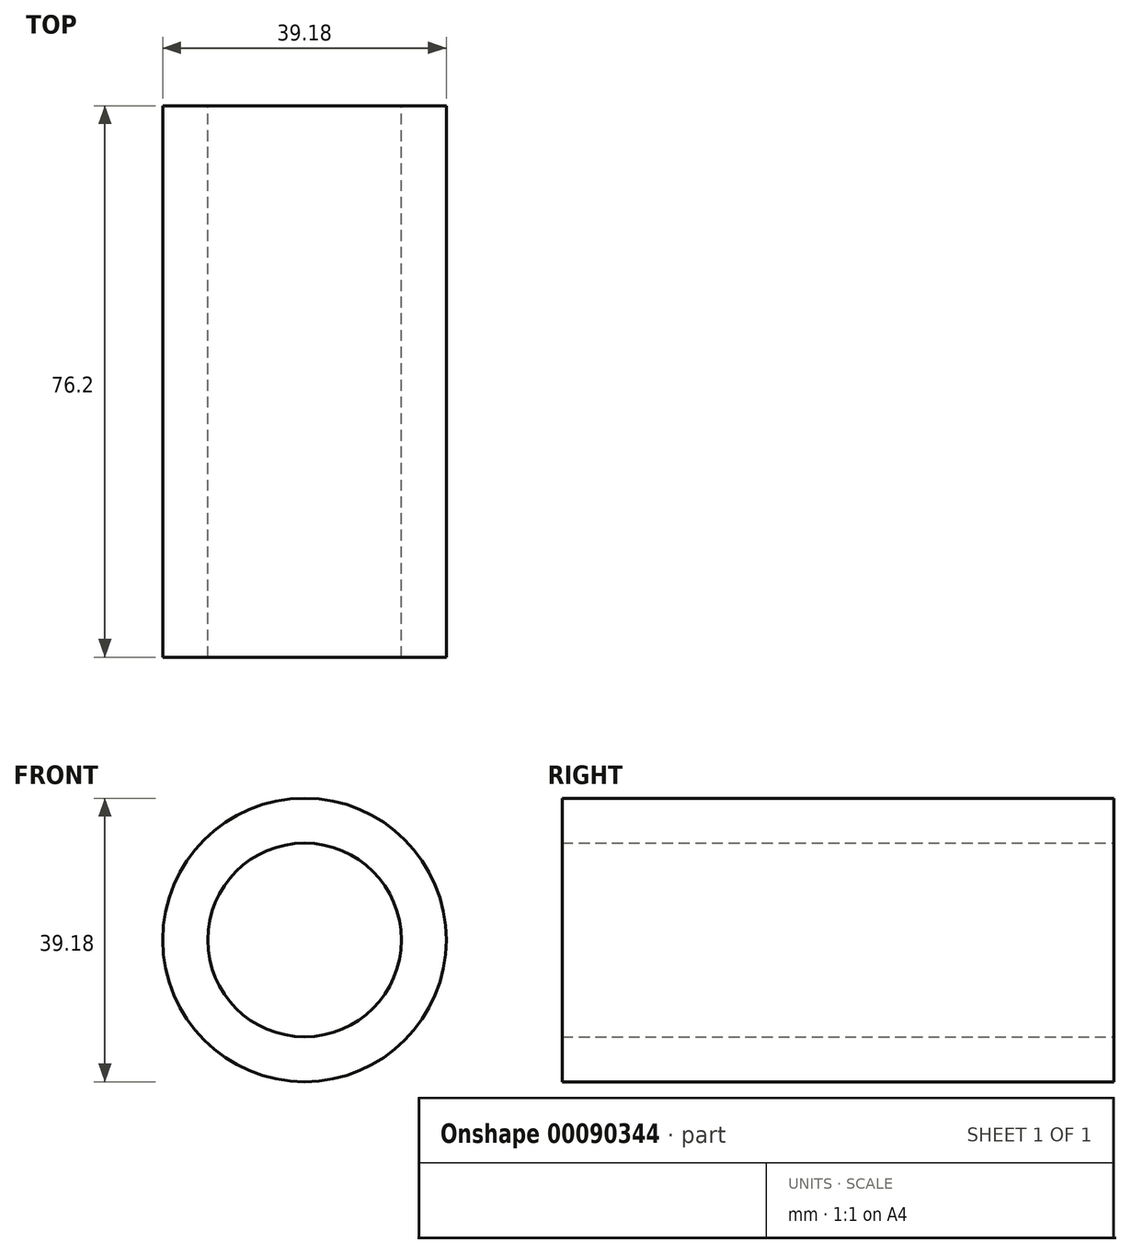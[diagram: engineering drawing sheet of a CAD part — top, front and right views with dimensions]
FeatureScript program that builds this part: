
annotation { "Feature Type Name" : "Feature", "Feature Type Description" : "" }
export const myFeature = defineFeature(function(context is Context, id is Id, definition is map)
    precondition{}
    {
        {
            var Q0;
            Q0=qCreatedBy(makeId("Front.planeOp"),FACE);
            var sketch = newSketch(context, id + "F0", { "sketchPlane" : qUnion([Q0])});
            skCircle(sketch, "E0", {"center": v(-105.88, 58.44) * mm, "radius": 19.59 * mm});
            skCircle(sketch, "E1", {"center": v(-105.88, 58.44) * mm, "radius": 13.38 * mm});
            skSolve(sketch);
        }
        {
            var Q0;
            Q0 = qSketchRegion(id + "F0", true);
            extrude(context, id + "F1", {"entities" : qUnion([Q0]), "depth" : 76.2 * mm});
        }
    });
